# Revit family: Bicycle-Racks_Huntco_Custom-LC
name_source: partatom
category: Site
units: mm (PartAtom-declared; Revit-internal decimal feet)

## family parameters
Classification Number = 23.40.10.11.11
Cut with Voids When Loaded = No
Host = Face
Part Type = Normal
Round Connector Dimension = Use Diameter
Shared = No

## types (9) — shared parameters
Assembly Code = G2040500
Capacity = Bike Capacity as Specified
Construction Details = http://www.arcat.com
Default Elevation = 4' - 0"
Embedded Mounted = No
Green Building-LEED = http://www.arcat.com
Keynote = 02871
Manufacturer = Huntco Supply LLC
Manufacturer Fax = 503-274-2055
Manufacturer Website = http://www.huntco.com
Pipe = Metal - Steel - Huntco - Stainless
Plate = Metal - Steel - Huntco - Stainless
Post = Metal - Steel - Huntco - Stainless
Product Data = http://www.arcat.com
Revision = R1_11_2012
Send Message = http://www.arcat.com
Specification = http://www.arcat.com
Surface Mounted = Yes
URL = http://www.huntco.com
Unit Depth = 0' - 2 1/2"
Unit Height = 3' - 10"
extralength = 0' - 0"
holedepth = 0' - 4"
holediameter = 0' - 0 1/2"
zero-valued in all types: Expected Lifespan (Years), Maintenance Schedule (Months), Unit Weight, Warranty Duration (Years)

## per-type parameters (varying)
| type | Description | No of Rods | Unit Width | rodcalc |
| LC14 | Huntco LC Series Bike Rack - Model LC14 | 15 | 8' - 0" | 15.454545 |
| LC13 | Huntco LC Series Bike Rack - Model LC13 | 14 | 7' - 6" | 14.363636 |
| LC12 | Huntco LC Series Bike Rack - Model LC12 | 13 | 7' - 0" | 13.272727 |
| LC11 | Huntco LC Series Bike Rack - Model LC11 | 12 | 6' - 6" | 12.181818 |
| LC10 | Huntco LC Series Bike Rack - Model LC10 | 11 | 6' - 0" | 11.090909 |
| LC9 | Huntco LC Series Bike Rack - Model LC9 | 10 | 5' - 6" | 10 |
| LC8 | Huntco LC Series Bike Rack - Model LC8 | 9 | 5' - 0" | 8.909091 |
| LC7 | Huntco LC Series Bike Rack - Model LC7 | 8 | 4' - 6" | 7.818182 |
| LC6 | Huntco LC Series Bike Rack - Model LC6 | 7 | 4' - 0" | 6.727273 |

note: column(s) folded — value = type name in every type: Model

## geometry (parser evidence)
native form markers: Blend x4, Sweep x4
no freeform markers — native parametric forms only
